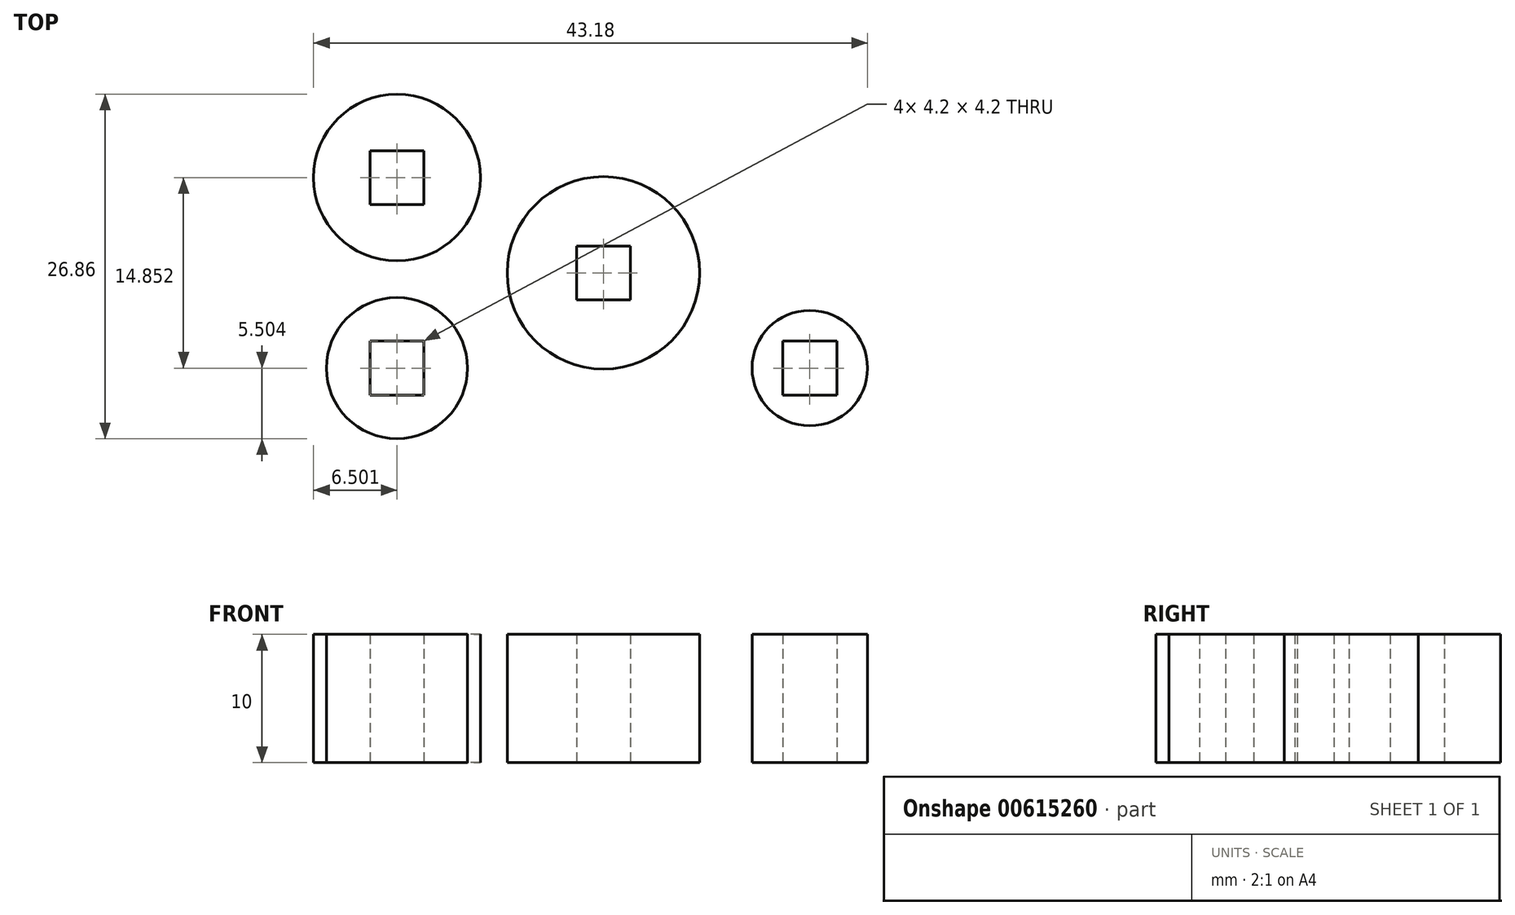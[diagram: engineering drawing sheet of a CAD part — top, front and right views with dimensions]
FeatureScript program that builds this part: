
annotation { "Feature Type Name" : "Feature", "Feature Type Description" : "" }
export const myFeature = defineFeature(function(context is Context, id is Id, definition is map)
    precondition{}
    {
        {
            var Q0;
            Q0=qCreatedBy(makeId("Top.planeOp"),FACE);
            var sketch = newSketch(context, id + "F0", { "sketchPlane" : qUnion([Q0])});
            skLineSegment(sketch, "E0.bottom", {"start": v(16.09, -7.43) * mm, "end": v(-16.09, -7.43) * mm, "construction": true});
            skLineSegment(sketch, "E0.top", {"start": v(16.09, 7.43) * mm, "end": v(-16.09, 7.43) * mm, "construction": true});
            skLineSegment(sketch, "E0.left", {"start": v(16.09, -7.43) * mm, "end": v(16.09, 7.43) * mm, "construction": true});
            skLineSegment(sketch, "E0.right", {"start": v(-16.09, -7.43) * mm, "end": v(-16.09, 7.43) * mm, "construction": true});
            skPoint(sketch, "E0.middle", {"position": v(0, 0) * mm});
            skCircle(sketch, "E1", {"center": v(-16.09, 7.43) * mm, "radius": 6.5 * mm});
            skCircle(sketch, "E2", {"center": v(-16.09, -7.43) * mm, "radius": 5.5 * mm});
            skCircle(sketch, "E3", {"center": v(16.09, -7.43) * mm, "radius": 4.5 * mm});
            skCircle(sketch, "E4", {"center": v(16.09, 7.43) * mm, "radius": 3.5 * mm});
            skCircle(sketch, "E5", {"center": v(0, 0) * mm, "radius": 7.5 * mm});
            skLineSegment(sketch, "E6.bottom", {"start": v(-13.99, 5.33) * mm, "end": v(-18.19, 5.33) * mm});
            skLineSegment(sketch, "E6.top", {"start": v(-13.99, 9.53) * mm, "end": v(-18.19, 9.53) * mm});
            skLineSegment(sketch, "E6.left", {"start": v(-13.99, 5.33) * mm, "end": v(-13.99, 9.53) * mm});
            skLineSegment(sketch, "E6.right", {"start": v(-18.19, 5.33) * mm, "end": v(-18.19, 9.53) * mm});
            skLineSegment(sketch, "E7.bottom", {"start": v(-13.99, -9.53) * mm, "end": v(-18.19, -9.53) * mm});
            skLineSegment(sketch, "E7.top", {"start": v(-13.99, -5.33) * mm, "end": v(-18.19, -5.33) * mm});
            skLineSegment(sketch, "E7.left", {"start": v(-13.99, -9.53) * mm, "end": v(-13.99, -5.33) * mm});
            skLineSegment(sketch, "E7.right", {"start": v(-18.19, -9.53) * mm, "end": v(-18.19, -5.33) * mm});
            skLineSegment(sketch, "E8.bottom", {"start": v(2.1, -2.1) * mm, "end": v(-2.1, -2.1) * mm});
            skLineSegment(sketch, "E8.top", {"start": v(2.1, 2.1) * mm, "end": v(-2.1, 2.1) * mm});
            skLineSegment(sketch, "E8.left", {"start": v(2.1, -2.1) * mm, "end": v(2.1, 2.1) * mm});
            skLineSegment(sketch, "E8.right", {"start": v(-2.1, -2.1) * mm, "end": v(-2.1, 2.1) * mm});
            skLineSegment(sketch, "E9.left", {"start": v(17.41, 4.19) * mm, "end": v(17.41, 9.59) * mm});
            skLineSegment(sketch, "E10.bottom", {"start": v(18.19, -9.53) * mm, "end": v(13.99, -9.53) * mm});
            skLineSegment(sketch, "E10.top", {"start": v(18.19, -5.33) * mm, "end": v(13.99, -5.33) * mm});
            skLineSegment(sketch, "E10.left", {"start": v(18.19, -9.53) * mm, "end": v(18.19, -5.33) * mm});
            skLineSegment(sketch, "E10.right", {"start": v(13.99, -9.53) * mm, "end": v(13.99, -5.33) * mm});
            skLineSegment(sketch, "E11.bottom", {"start": v(18.19, 5.33) * mm, "end": v(13.99, 5.33) * mm});
            skLineSegment(sketch, "E11.top", {"start": v(18.19, 9.53) * mm, "end": v(13.99, 9.53) * mm});
            skLineSegment(sketch, "E11.left", {"start": v(18.19, 5.33) * mm, "end": v(18.19, 9.53) * mm});
            skLineSegment(sketch, "E11.right", {"start": v(13.99, 5.33) * mm, "end": v(13.99, 9.53) * mm});
            skSolve(sketch);
        }
        {
            var Q0;
            Q0=makeQuery(id+"F0.imprint","IMPRINT",FACE,{"disambiguationData":[TD([[makeQuery(id+"F0.imprint","IMPRINT",EDGE,{"derivedFrom":sQuery(id+"F0.wireOp",EDGE,"E1")}),1.0]])]});
            var Q1;
            Q1=makeQuery(id+"F0.imprint","IMPRINT",FACE,{"disambiguationData":[TD([[makeQuery(id+"F0.imprint","IMPRINT",EDGE,{"derivedFrom":sQuery(id+"F0.wireOp",EDGE,"E2")}),1.0]])]});
            var Q2;
            Q2=makeQuery(id+"F0.imprint","IMPRINT",FACE,{"disambiguationData":[TD([[makeQuery(id+"F0.imprint","IMPRINT",EDGE,{"derivedFrom":sQuery(id+"F0.wireOp",EDGE,"E5")}),1.0]])]});
            var Q3;
            Q3=makeQuery(id+"F0.imprint","IMPRINT",FACE,{"disambiguationData":[TD([[makeQuery(id+"F0.imprint","IMPRINT",EDGE,{"derivedFrom":sQuery(id+"F0.wireOp",EDGE,"E3")}),1.0]])]});
            extrude(context, id + "F1", {"entities" : qUnion([Q0, Q1, Q2, Q3]), "depth" : 10 * mm, "offsetDistance" : 25 * mm});
        }
    });
